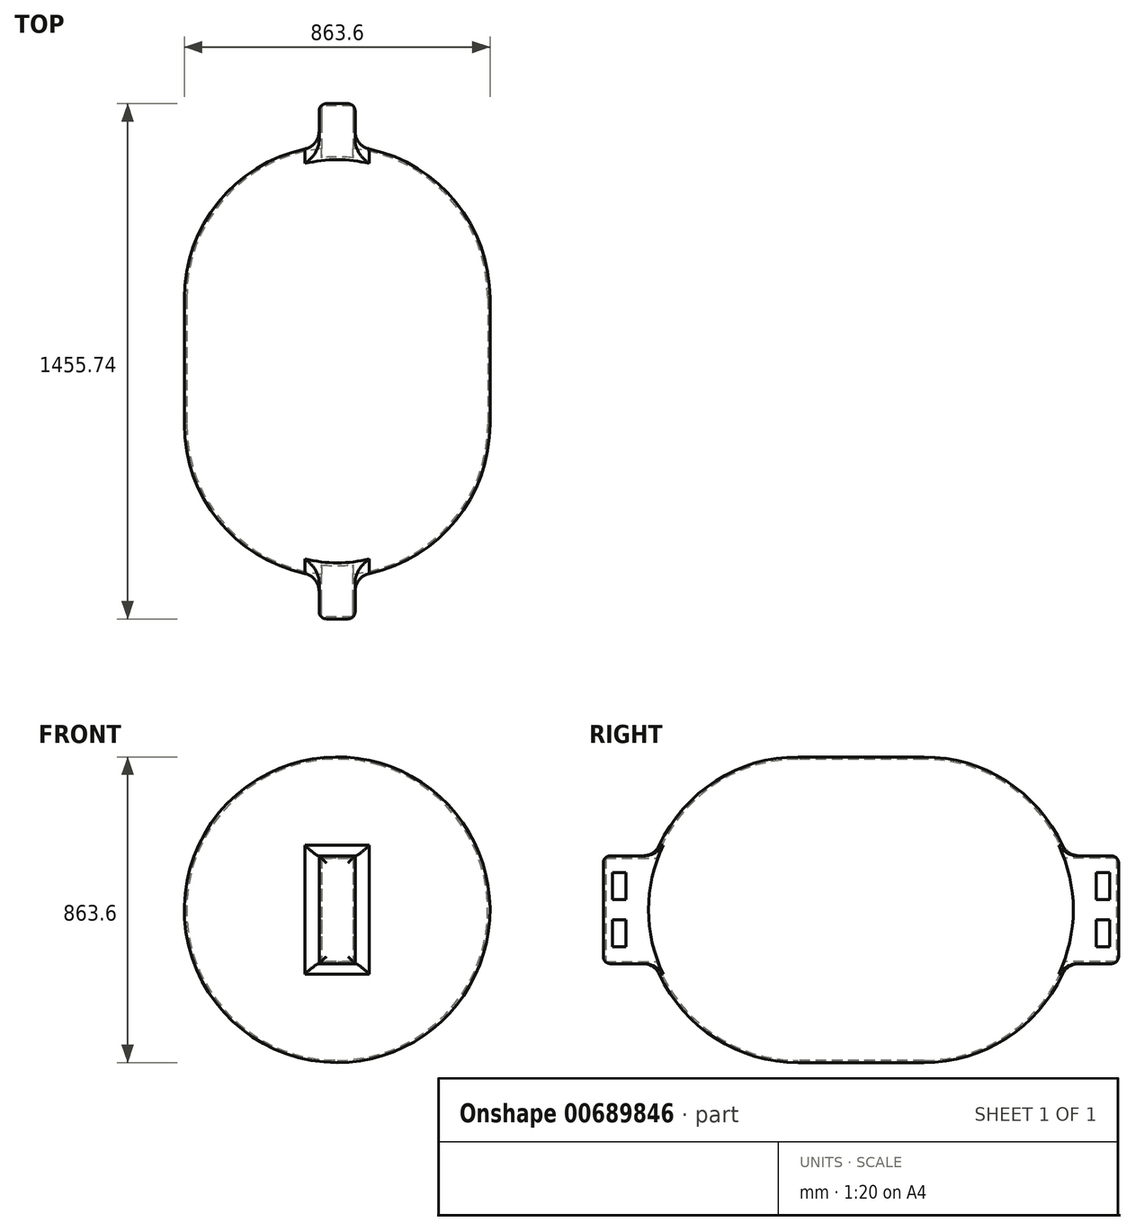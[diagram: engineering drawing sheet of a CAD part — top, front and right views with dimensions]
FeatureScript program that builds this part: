
annotation { "Feature Type Name" : "Feature", "Feature Type Description" : "" }
export const myFeature = defineFeature(function(context is Context, id is Id, definition is map)
    precondition{}
    {
        {
            var Q0;
            Q0=qCreatedBy(makeId("Right.planeOp"),FACE);
            var sketch = newSketch(context, id + "F0", { "sketchPlane" : qUnion([Q0])});
            skLineSegment(sketch, "E0", {"start": v(0, 431.8) * mm, "end": v(0, 0) * mm});
            skLineSegment(sketch, "E1", {"start": v(0, 431.8) * mm, "end": v(-177.8, 431.8) * mm});
            skArc(sketch, "E2", {"start": v(-177.8, 431.8) * mm, "mid": v(-483.13, 305.33) * mm, "end": v(-609.6, 0) * mm});
            skLineSegment(sketch, "E3", {"start": v(-177.8, 0) * mm, "end": v(0, 0) * mm, "construction": true});
            skLineSegment(sketch, "E4", {"start": v(-609.6, 0) * mm, "end": v(0, 0) * mm});
            skPoint(sketch, "E5.end.orphan", {"position": v(-177.8, -431.8) * mm});
            skPoint(sketch, "E6.orphan", {"position": v(0, -431.8) * mm});
            skSolve(sketch);
        }
        {
            var Q0;
            Q0 = qSketchRegion(id + "F0", true);
            var Q1;
            Q1=sQuery(id+"F0.wireOp",EDGE,"E4");
            revolve(context, id + "F1", {"surfaceOperationType" : NewSurfaceOperationType.NEW, "entities" : qUnion([Q0]), "axis" : qUnion([Q1]), "revolveType" : RevolveType.FULL});
        }
        {
            var Q0;
            Q0=qCreatedBy(makeId("Right.planeOp"),FACE);
            var sketch = newSketch(context, id + "F2", { "sketchPlane" : qUnion([Q0])});
            skLineSegment(sketch, "E7.bottom", {"start": v(-727.87, 152.4) * mm, "end": v(-550.07, 152.4) * mm});
            skLineSegment(sketch, "E7.top", {"start": v(-727.87, -152.4) * mm, "end": v(-550.07, -152.4) * mm});
            skLineSegment(sketch, "E7.left", {"start": v(-727.87, 152.4) * mm, "end": v(-727.87, -152.4) * mm});
            skLineSegment(sketch, "E7.right", {"start": v(-550.07, 152.4) * mm, "end": v(-550.07, -152.4) * mm});
            skLineSegment(sketch, "E8", {"start": v(-550.07, 0) * mm, "end": v(0, 0) * mm, "construction": true});
            skSolve(sketch);
        }
        {
            var Q0;
            Q0 = qSketchRegion(id + "F2", true);
            extrude(context, id + "F3", {"entities" : qUnion([Q0]), "operationType" : NewBodyOperationType.ADD, "endBound" : BoundingType.SYMMETRIC, "depth" : 101.6 * mm, "offsetDistance" : 25.4 * mm});
        }
        {
            var Q0;
            Q0=makeQuery(id+"F1.opRevolve","SWEPT_FACE",FACE,{"disambiguationData":[OSD([sQuery(id+"F0.wireOp",EDGE,"E0")])]});
            shell(context, id + "F4", {"entities" : qUnion([Q0]), "thickness" : 6.35 * mm});
        }
        {
            var Q0;
            Q0=makeQuery(id+"F3.boolean.opBoolean","INTERSECT",EDGE,{"derivedFrom":[makeQuery(id+"F1.opRevolve","SWEPT_FACE",FACE,{"disambiguationData":[OSD([sQuery(id+"F0.wireOp",EDGE,"E2")])]}),makeQuery(id+"F3.opExtrude","CAP_FACE",FACE,{"disambiguationData":[OSD([sQuery(id+"F2.wireOp",EDGE,"E7.bottom"),sQuery(id+"F2.wireOp",EDGE,"E7.top"),sQuery(id+"F2.wireOp",EDGE,"E7.left"),sQuery(id+"F2.wireOp",EDGE,"E7.right")])],"isStart":false})]});
            var Q1;
            Q1=makeQuery(id+"F3.boolean.opBoolean","INTERSECT",EDGE,{"derivedFrom":[makeQuery(id+"F1.opRevolve","SWEPT_FACE",FACE,{"disambiguationData":[OSD([sQuery(id+"F0.wireOp",EDGE,"E2")])]}),makeQuery(id+"F3.opExtrude","SWEPT_FACE",FACE,{"disambiguationData":[OSD([sQuery(id+"F2.wireOp",EDGE,"E7.bottom")])]})]});
            var Q2;
            Q2=makeQuery(id+"F3.boolean.opBoolean","INTERSECT",EDGE,{"derivedFrom":[makeQuery(id+"F1.opRevolve","SWEPT_FACE",FACE,{"disambiguationData":[OSD([sQuery(id+"F0.wireOp",EDGE,"E2")])]}),makeQuery(id+"F3.opExtrude","CAP_FACE",FACE,{"disambiguationData":[OSD([sQuery(id+"F2.wireOp",EDGE,"E7.bottom"),sQuery(id+"F2.wireOp",EDGE,"E7.top"),sQuery(id+"F2.wireOp",EDGE,"E7.left"),sQuery(id+"F2.wireOp",EDGE,"E7.right")])],"isStart":true})]});
            var Q3;
            Q3=makeQuery(id+"F3.boolean.opBoolean","INTERSECT",EDGE,{"derivedFrom":[makeQuery(id+"F1.opRevolve","SWEPT_FACE",FACE,{"disambiguationData":[OSD([sQuery(id+"F0.wireOp",EDGE,"E2")])]}),makeQuery(id+"F3.opExtrude","SWEPT_FACE",FACE,{"disambiguationData":[OSD([sQuery(id+"F2.wireOp",EDGE,"E7.top")])]})]});
            fillet(context, id + "F5", {"entities" : qUnion([Q0, Q1, Q2, Q3]), "tangentPropagation" : true, "radius" : 50.8 * mm, "defaultsChanged" : true, "vertexSettings" : [], "allowEdgeOverflow" : false});
        }
        {
            var Q0;
            Q0=makeQuery(id+"F3.opExtrude","SWEPT_EDGE",EDGE,{"disambiguationData":[OSD([sQuery(id+"F2.wireOp",EDGE,"E7.top"),sQuery(id+"F2.wireOp",EDGE,"E7.left")])]});
            var Q1;
            Q1=makeQuery(id+"F3.opExtrude","SWEPT_EDGE",EDGE,{"disambiguationData":[OSD([sQuery(id+"F2.wireOp",EDGE,"E7.bottom"),sQuery(id+"F2.wireOp",EDGE,"E7.left")])]});
            var Q2;
            Q2=makeQuery(id+"F3.opExtrude","CAP_EDGE",EDGE,{"disambiguationData":[OSD([sQuery(id+"F2.wireOp",EDGE,"E7.left")])],"isStart":true});
            var Q3;
            Q3=makeQuery(id+"F3.opExtrude","CAP_EDGE",EDGE,{"disambiguationData":[OSD([sQuery(id+"F2.wireOp",EDGE,"E7.left")])],"isStart":false});
            fillet(context, id + "F6", {"entities" : qUnion([Q0, Q1, Q2, Q3]), "tangentPropagation" : true, "radius" : 20.32 * mm, "defaultsChanged" : true, "vertexSettings" : [], "allowEdgeOverflow" : false});
        }
        {
            var Q0;
            Q0=qCreatedBy(makeId("Right.planeOp"),FACE);
            var sketch = newSketch(context, id + "F7", { "sketchPlane" : qUnion([Q0])});
            skLineSegment(sketch, "E9.bottom", {"start": v(-702.47, 105.02) * mm, "end": v(-664.37, 105.02) * mm});
            skLineSegment(sketch, "E9.top", {"start": v(-702.47, 28.82) * mm, "end": v(-664.37, 28.82) * mm});
            skLineSegment(sketch, "E9.left", {"start": v(-702.47, 105.02) * mm, "end": v(-702.47, 28.82) * mm});
            skLineSegment(sketch, "E9.right", {"start": v(-664.37, 105.02) * mm, "end": v(-664.37, 28.82) * mm});
            skLineSegment(sketch, "E10.bottom", {"start": v(-702.47, -28.82) * mm, "end": v(-664.37, -28.82) * mm});
            skLineSegment(sketch, "E10.top", {"start": v(-702.47, -105.02) * mm, "end": v(-664.37, -105.02) * mm});
            skLineSegment(sketch, "E10.left", {"start": v(-702.47, -28.82) * mm, "end": v(-702.47, -105.02) * mm});
            skLineSegment(sketch, "E10.right", {"start": v(-664.37, -28.82) * mm, "end": v(-664.37, -105.02) * mm});
            skLineSegment(sketch, "E11", {"start": v(-702.47, 28.82) * mm, "end": v(-702.47, -28.82) * mm, "construction": true});
            skLineSegment(sketch, "E12", {"start": v(-702.47, 0) * mm, "end": v(0, 0) * mm, "construction": true});
            skSolve(sketch);
        }
        {
            var Q0;
            Q0 = qSketchRegion(id + "F7", true);
            extrude(context, id + "F8", {"entities" : qUnion([Q0]), "operationType" : NewBodyOperationType.REMOVE, "endBound" : BoundingType.SYMMETRIC, "oppositeDirection" : true, "depth" : 1016 * mm, "offsetDistance" : 25.4 * mm});
        }
        {
            var Q0;
            Q0=makeQuery(id+"F1.opRevolve","SWEPT_BODY",BODY,{"disambiguationData":[OSD([sQuery(id+"F0.wireOp",EDGE,"E0"),sQuery(id+"F0.wireOp",EDGE,"E1"),sQuery(id+"F0.wireOp",EDGE,"E2"),sQuery(id+"F0.wireOp",EDGE,"E4")])]});
            var Q1;
            Q1=qCreatedBy(makeId("Front.planeOp"),FACE);
            mirror(context, id + "F9", {"operationType" : NewBodyOperationType.ADD, "entities" : qUnion([Q0]), "mirrorPlane" : qUnion([Q1])});
        }
    });
